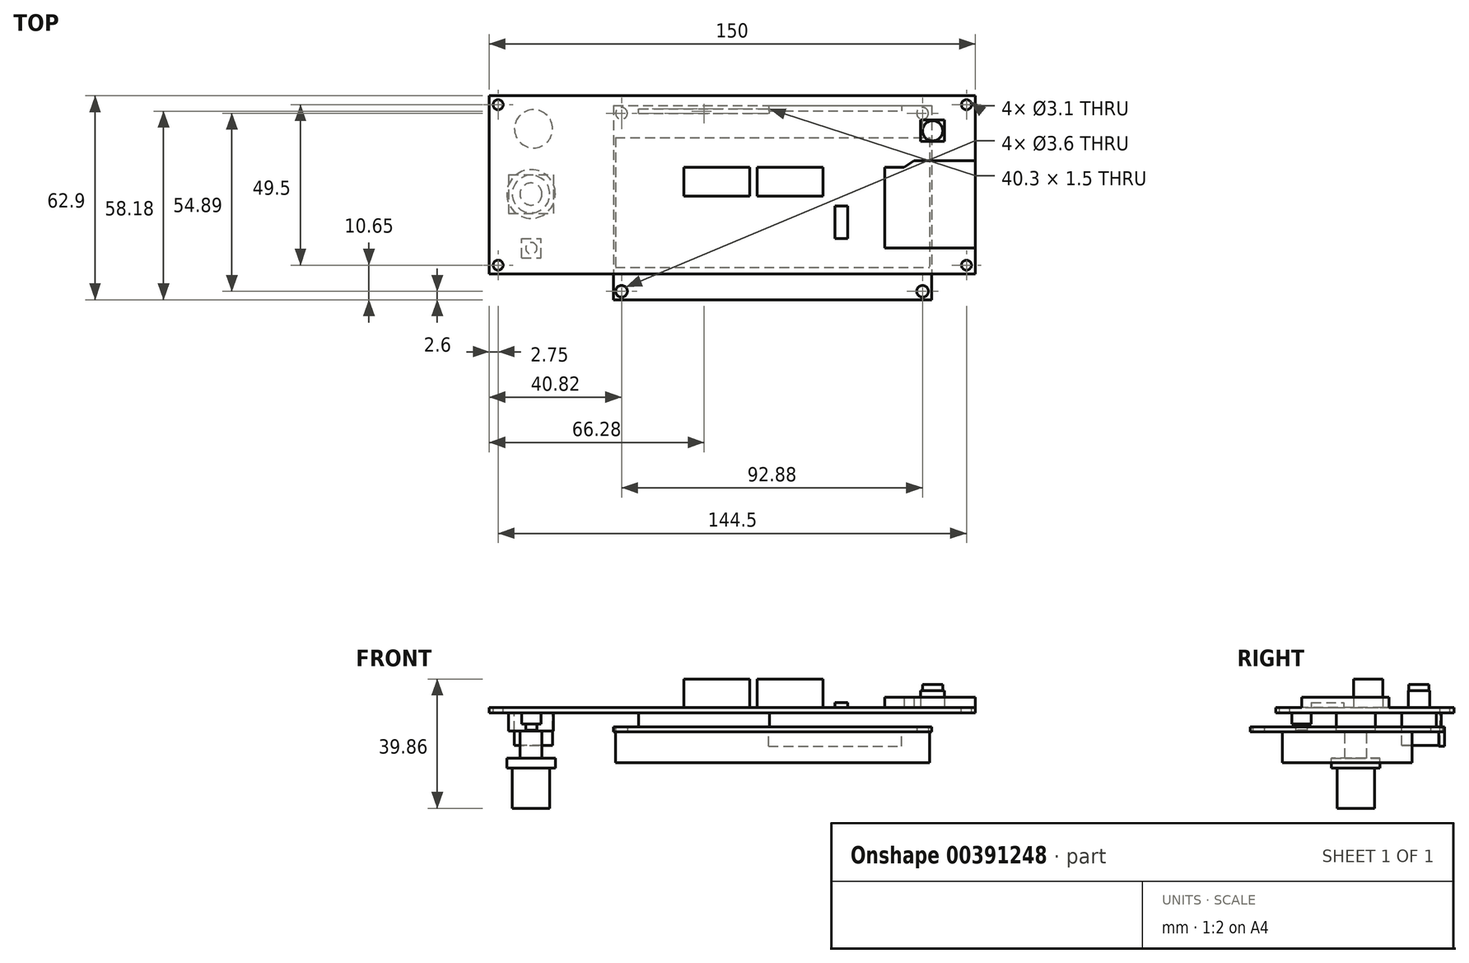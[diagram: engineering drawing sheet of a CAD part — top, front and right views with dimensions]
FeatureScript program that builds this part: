
annotation { "Feature Type Name" : "Feature", "Feature Type Description" : "" }
export const myFeature = defineFeature(function(context is Context, id is Id, definition is map)
    precondition{}
    {
        {
            var Q0;
            Q0=qCreatedBy(makeId("Top.planeOp"),FACE);
            var sketch = newSketch(context, id + "F0", { "sketchPlane" : qUnion([Q0])});
            skLineSegment(sketch, "E0.bottom", {"start": v(0, 0) * mm, "end": v(150, 0) * mm});
            skLineSegment(sketch, "E0.top", {"start": v(0, 55) * mm, "end": v(150, 55) * mm});
            skLineSegment(sketch, "E0.left", {"start": v(0, 0) * mm, "end": v(0, 55) * mm});
            skLineSegment(sketch, "E0.right", {"start": v(150, 0) * mm, "end": v(150, 55) * mm});
            skCircle(sketch, "E1", {"center": v(2.75, 52.25) * mm, "radius": 1.55 * mm});
            skCircle(sketch, "E2", {"center": v(2.75, 2.75) * mm, "radius": 1.55 * mm});
            skCircle(sketch, "E3", {"center": v(147.25, 52.25) * mm, "radius": 1.55 * mm});
            skCircle(sketch, "E4", {"center": v(147.25, 2.75) * mm, "radius": 1.55 * mm});
            skLineSegment(sketch, "E5.bottom", {"start": v(60, 24) * mm, "end": v(80.36, 24) * mm});
            skLineSegment(sketch, "E5.top", {"start": v(60, 33) * mm, "end": v(80.36, 33) * mm});
            skLineSegment(sketch, "E5.left", {"start": v(60, 24) * mm, "end": v(60, 33) * mm});
            skLineSegment(sketch, "E5.right", {"start": v(103, 24) * mm, "end": v(103, 33) * mm});
            skPoint(sketch, "E6", {"position": v(150, 8) * mm});
            skPoint(sketch, "E7", {"position": v(150, 35) * mm});
            skPoint(sketch, "E8", {"position": v(131, 35) * mm});
            skPoint(sketch, "E9", {"position": v(122, 8) * mm});
            skPoint(sketch, "E10", {"position": v(122, 33) * mm});
            skPoint(sketch, "E11", {"position": v(128, 33) * mm});
            skLineSegment(sketch, "E12", {"start": v(122, 33) * mm, "end": v(128, 33) * mm});
            skLineSegment(sketch, "E13", {"start": v(131, 35) * mm, "end": v(128, 33) * mm});
            skLineSegment(sketch, "E14", {"start": v(150, 35) * mm, "end": v(131, 35) * mm});
            skLineSegment(sketch, "E15", {"start": v(122, 33) * mm, "end": v(122, 8) * mm});
            skLineSegment(sketch, "E16", {"start": v(122, 8) * mm, "end": v(150, 8) * mm});
            skLineSegment(sketch, "E17", {"start": v(2.75, 52.25) * mm, "end": v(2.75, 2.75) * mm, "construction": true});
            skLineSegment(sketch, "E18", {"start": v(2.75, 2.75) * mm, "end": v(147.25, 2.75) * mm, "construction": true});
            skLineSegment(sketch, "E19", {"start": v(147.25, 2.75) * mm, "end": v(147.25, 52.25) * mm, "construction": true});
            skLineSegment(sketch, "E20", {"start": v(147.25, 52.25) * mm, "end": v(2.75, 52.25) * mm, "construction": true});
            skCircle(sketch, "E21", {"center": v(136.8, 44.2) * mm, "radius": 3.12 * mm});
            skLineSegment(sketch, "E22.bottom", {"start": v(140.5, 40.9) * mm, "end": v(133.1, 40.9) * mm});
            skLineSegment(sketch, "E22.top", {"start": v(140.5, 47.5) * mm, "end": v(133.1, 47.5) * mm});
            skLineSegment(sketch, "E22.left", {"start": v(140.5, 40.9) * mm, "end": v(140.5, 47.5) * mm});
            skLineSegment(sketch, "E22.right", {"start": v(133.1, 40.9) * mm, "end": v(133.1, 47.5) * mm});
            skLineSegment(sketch, "E23.bottom", {"start": v(106.7, 11) * mm, "end": v(110.6, 11) * mm});
            skLineSegment(sketch, "E23.top", {"start": v(106.7, 21) * mm, "end": v(110.6, 21) * mm});
            skLineSegment(sketch, "E23.left", {"start": v(106.7, 11) * mm, "end": v(106.7, 21) * mm});
            skLineSegment(sketch, "E23.right", {"start": v(110.6, 11) * mm, "end": v(110.6, 21) * mm});
            skLineSegment(sketch, "E24", {"start": v(80.36, 33) * mm, "end": v(80.36, 24) * mm});
            skLineSegment(sketch, "E25", {"start": v(82.64, 33) * mm, "end": v(82.64, 24) * mm});
            skLineSegment(sketch, "E26.trimOffspring", {"start": v(82.64, 33) * mm, "end": v(103, 33) * mm});
            skLineSegment(sketch, "E27.trimOffspring", {"start": v(82.64, 24) * mm, "end": v(103, 24) * mm});
            skSolve(sketch);
        }
        {
            var Q0;
            Q0 = qSketchRegion(id + "F0", true);
            var Q1;
            Q1=makeQuery(id+"F0.imprint","IMPRINT",FACE,{"disambiguationData":[TD([[makeQuery(id+"F0.imprint","IMPRINT",EDGE,{"derivedFrom":sQuery(id+"F0.wireOp",EDGE,"E5.bottom")}),1.0]])]});
            var Q2;
            Q2=makeQuery(id+"F0.imprint","IMPRINT",FACE,{"disambiguationData":[TD([[makeQuery(id+"F0.imprint","IMPRINT",EDGE,{"derivedFrom":sQuery(id+"F0.wireOp",EDGE,"E23.bottom")}),1.0]])]});
            var Q3;
            Q3=makeQuery(id+"F0.imprint","IMPRINT",FACE,{"disambiguationData":[TD([[makeQuery(id+"F0.imprint","IMPRINT",EDGE,{"derivedFrom":sQuery(id+"F0.wireOp",EDGE,"E21")}),-1.0]])]});
            var Q4;
            Q4=makeQuery(id+"F0.imprint","IMPRINT",FACE,{"disambiguationData":[TD([[makeQuery(id+"F0.imprint","IMPRINT",EDGE,{"derivedFrom":sQuery(id+"F0.wireOp",EDGE,"E21")}),1.0]])]});
            var Q5;
            Q5=makeQuery(id+"F0.imprint","IMPRINT",FACE,{"disambiguationData":[TD([[makeQuery(id+"F0.imprint","IMPRINT",EDGE,{"derivedFrom":sQuery(id+"F0.wireOp",EDGE,"E5.right")}),1.0]])]});
            extrude(context, id + "F1", {"entities" : qUnion([Q0, Q1, Q2, Q3, Q4, Q5]), "oppositeDirection" : true, "depth" : 1.6 * mm});
        }
        {
            var Q0;
            Q0=makeQuery(id+"F0.imprint","IMPRINT",FACE,{"disambiguationData":[TD([[makeQuery(id+"F0.imprint","IMPRINT",EDGE,{"derivedFrom":sQuery(id+"F0.wireOp",EDGE,"E5.bottom")}),1.0]])]});
            var Q1;
            Q1=makeQuery(id+"F0.imprint","IMPRINT",FACE,{"disambiguationData":[TD([[makeQuery(id+"F0.imprint","IMPRINT",EDGE,{"derivedFrom":sQuery(id+"F0.wireOp",EDGE,"E5.right")}),1.0]])]});
            extrude(context, id + "F2", {"entities" : qUnion([Q0, Q1]), "operationType" : NewBodyOperationType.ADD, "depth" : 8.8 * mm});
        }
        {
            var Q0;
            Q0=makeQuery(id+"F0.imprint","IMPRINT",FACE,{"disambiguationData":[TD([[makeQuery(id+"F0.imprint","IMPRINT",EDGE,{"derivedFrom":sQuery(id+"F0.wireOp",EDGE,"E12")}),-1.0]])]});
            extrude(context, id + "F3", {"entities" : qUnion([Q0]), "operationType" : NewBodyOperationType.ADD, "depth" : 3.2 * mm});
        }
        {
            var Q0;
            Q0=makeQuery(id+"F0.imprint","IMPRINT",FACE,{"disambiguationData":[TD([[makeQuery(id+"F0.imprint","IMPRINT",EDGE,{"derivedFrom":sQuery(id+"F0.wireOp",EDGE,"E23.bottom")}),1.0]])]});
            extrude(context, id + "F4", {"entities" : qUnion([Q0]), "operationType" : NewBodyOperationType.ADD, "depth" : 1.5 * mm});
        }
        {
            var Q0;
            Q0=makeQuery(id+"F0.imprint","IMPRINT",FACE,{"disambiguationData":[TD([[makeQuery(id+"F0.imprint","IMPRINT",EDGE,{"derivedFrom":sQuery(id+"F0.wireOp",EDGE,"E21")}),-1.0]])]});
            var Q1;
            Q1=makeQuery(id+"F0.imprint","IMPRINT",FACE,{"disambiguationData":[TD([[makeQuery(id+"F0.imprint","IMPRINT",EDGE,{"derivedFrom":sQuery(id+"F0.wireOp",EDGE,"E21")}),1.0]])]});
            extrude(context, id + "F5", {"entities" : qUnion([Q0, Q1]), "operationType" : NewBodyOperationType.ADD, "depth" : 5.3 * mm});
        }
        {
            var Q0;
            Q0=makeQuery(id+"F5.opExtrude","CAP_FACE",FACE,{"disambiguationData":[OSD([sQuery(id+"F0.wireOp",EDGE,"E22.bottom"),sQuery(id+"F0.wireOp",EDGE,"E22.top"),sQuery(id+"F0.wireOp",EDGE,"E22.left"),sQuery(id+"F0.wireOp",EDGE,"E22.right")])],"isStart":false});
            var sketch = newSketch(context, id + "F6", { "sketchPlane" : qUnion([Q0])});
            skCircle(sketch, "E28.1", {"center": v(136.8, 44.2) * mm, "radius": 3.12 * mm});
            skSolve(sketch);
        }
        {
            var Q0;
            Q0=makeQuery(id+"F6.imprint","IMPRINT",FACE,{"disambiguationData":[TD([[makeQuery(id+"F6.imprint","IMPRINT",EDGE,{"derivedFrom":sQuery(id+"F6.wireOp",EDGE,"E28.1")}),1.0]])]});
            extrude(context, id + "F7", {"entities" : qUnion([Q0]), "operationType" : NewBodyOperationType.ADD, "depth" : 1.87 * mm});
        }
        {
            var Q0;
            Q0=makeQuery(id+"F1.opExtrude","CAP_FACE",FACE,{"disambiguationData":[OSD([sQuery(id+"F0.wireOp",EDGE,"E0.bottom"),sQuery(id+"F0.wireOp",EDGE,"E0.top"),sQuery(id+"F0.wireOp",EDGE,"E0.left"),sQuery(id+"F0.wireOp",EDGE,"E0.right"),sQuery(id+"F0.wireOp",EDGE,"E1"),sQuery(id+"F0.wireOp",EDGE,"E2"),sQuery(id+"F0.wireOp",EDGE,"E3"),sQuery(id+"F0.wireOp",EDGE,"E4")])],"isStart":false});
            var sketch = newSketch(context, id + "F8", { "sketchPlane" : qUnion([Q0])});
            skCircle(sketch, "E29", {"center": v(13.68, -44.82) * mm, "radius": 5.88 * mm});
            skSolve(sketch);
        }
        {
            var Q0;
            Q0=makeQuery(id+"F8.imprint","IMPRINT",FACE,{"disambiguationData":[TD([[makeQuery(id+"F8.imprint","IMPRINT",EDGE,{"derivedFrom":sQuery(id+"F8.wireOp",EDGE,"E29")}),1.0]])]});
            extrude(context, id + "F9", {"entities" : qUnion([Q0]), "operationType" : NewBodyOperationType.ADD, "depth" : 10 * mm});
        }
        {
            var Q0;
            Q0=makeQuery(id+"F1.opExtrude","CAP_FACE",FACE,{"disambiguationData":[OSD([sQuery(id+"F0.wireOp",EDGE,"E0.bottom"),sQuery(id+"F0.wireOp",EDGE,"E0.top"),sQuery(id+"F0.wireOp",EDGE,"E0.left"),sQuery(id+"F0.wireOp",EDGE,"E0.right"),sQuery(id+"F0.wireOp",EDGE,"E1"),sQuery(id+"F0.wireOp",EDGE,"E2"),sQuery(id+"F0.wireOp",EDGE,"E3"),sQuery(id+"F0.wireOp",EDGE,"E4")])],"isStart":false});
            var sketch = newSketch(context, id + "F10", { "sketchPlane" : qUnion([Q0])});
            skLineSegment(sketch, "E30.bottom", {"start": v(6, -30.7) * mm, "end": v(19.8, -30.7) * mm});
            skLineSegment(sketch, "E30.top", {"start": v(6, -18.7) * mm, "end": v(19.8, -18.7) * mm});
            skLineSegment(sketch, "E30.left", {"start": v(6, -30.7) * mm, "end": v(6, -18.7) * mm});
            skLineSegment(sketch, "E30.right", {"start": v(19.8, -30.7) * mm, "end": v(19.8, -18.7) * mm});
            skLineSegment(sketch, "E31.bottom", {"start": v(10, -5) * mm, "end": v(16, -5) * mm});
            skLineSegment(sketch, "E31.top", {"start": v(10, -11) * mm, "end": v(16, -11) * mm});
            skLineSegment(sketch, "E31.left", {"start": v(10, -5) * mm, "end": v(10, -11) * mm});
            skLineSegment(sketch, "E31.right", {"start": v(16, -5) * mm, "end": v(16, -11) * mm});
            skCircle(sketch, "E32", {"center": v(13, -8) * mm, "radius": 1.75 * mm});
            skPoint(sketch, "E32.centerSnap0", {"position": v(13, -5) * mm});
            skPoint(sketch, "E32.centerSnap1", {"position": v(10, -8) * mm});
            skCircle(sketch, "E33", {"center": v(12.9, -24.7) * mm, "radius": 7.5 * mm, "construction": true});
            skPoint(sketch, "E33.centerSnap0", {"position": v(6, -24.7) * mm});
            skPoint(sketch, "E33.centerSnap1", {"position": v(12.9, -18.7) * mm});
            skCircle(sketch, "E34", {"center": v(12.9, -24.7) * mm, "radius": 5.8 * mm, "construction": true});
            skSolve(sketch);
        }
        {
            var Q0;
            Q0=makeQuery(id+"F10.imprint","IMPRINT",FACE,{"disambiguationData":[TD([[makeQuery(id+"F10.imprint","IMPRINT",EDGE,{"derivedFrom":sQuery(id+"F10.wireOp",EDGE,"E30.bottom")}),1.0]])]});
            extrude(context, id + "F11", {"entities" : qUnion([Q0]), "operationType" : NewBodyOperationType.ADD, "depth" : 5.6 * mm});
        }
        {
            var Q0;
            Q0=makeQuery(id+"F11.opExtrude","CAP_FACE",FACE,{"disambiguationData":[OSD([sQuery(id+"F10.wireOp",EDGE,"E30.bottom"),sQuery(id+"F10.wireOp",EDGE,"E30.top"),sQuery(id+"F10.wireOp",EDGE,"E30.left"),sQuery(id+"F10.wireOp",EDGE,"E30.right")])],"isStart":false});
            var sketch = newSketch(context, id + "F12", { "sketchPlane" : qUnion([Q0])});
            skCircle(sketch, "E35", {"center": v(12.9, -24.7) * mm, "radius": 3.4 * mm});
            skPoint(sketch, "E35.centerSnap0", {"position": v(6, -24.7) * mm});
            skPoint(sketch, "E35.centerSnap1", {"position": v(12.9, -18.7) * mm});
            skSolve(sketch);
        }
        {
            var Q0;
            Q0 = qSketchRegion(id + "F12", true);
            extrude(context, id + "F13", {"entities" : qUnion([Q0]), "operationType" : NewBodyOperationType.ADD, "depth" : 8.4 * mm});
        }
        {
            var Q0;
            Q0=makeQuery(id+"F13.opExtrude","CAP_FACE",FACE,{"disambiguationData":[OSD([sQuery(id+"F12.wireOp",EDGE,"E35")])],"isStart":false});
            var sketch = newSketch(context, id + "F14", { "sketchPlane" : qUnion([Q0])});
            skCircle(sketch, "E36.0", {"center": v(12.9, -24.7) * mm, "radius": 7.5 * mm});
            skSolve(sketch);
        }
        {
            var Q0;
            Q0=makeQuery(id+"F14.imprint","IMPRINT",FACE,{"disambiguationData":[TD([[makeQuery(id+"F14.imprint","IMPRINT",EDGE,{"derivedFrom":sQuery(id+"F14.wireOp",EDGE,"E36.0")}),1.0]])]});
            var Q1;
            Q1=makeQuery(id+"F14.imprint","IMPRINT",FACE,{"disambiguationData":[TD([[makeQuery(id+"F14.imprint","IMPRINT",EDGE,{"derivedFrom":makeQuery(id+"F13.opExtrude","CAP_EDGE",EDGE,{"disambiguationData":[OSD([sQuery(id+"F12.wireOp",EDGE,"E35")])],"isStart":false})}),1.0]])]});
            extrude(context, id + "F15", {"entities" : qUnion([Q0, Q1]), "operationType" : NewBodyOperationType.ADD, "depth" : 3 * mm});
        }
        {
            var Q0;
            Q0=makeQuery(id+"F15.opExtrude","CAP_FACE",FACE,{"disambiguationData":[OSD([sQuery(id+"F14.wireOp",EDGE,"E36.0")])],"isStart":false});
            var sketch = newSketch(context, id + "F16", { "sketchPlane" : qUnion([Q0])});
            skCircle(sketch, "E37.0", {"center": v(12.9, -24.7) * mm, "radius": 5.8 * mm});
            skLineSegment(sketch, "E38.0", {"start": v(0, 0) * mm, "end": v(0, -55) * mm});
            skSolve(sketch);
        }
        {
            var Q0;
            Q0 = qSketchRegion(id + "F16", true);
            extrude(context, id + "F17", {"entities" : qUnion([Q0]), "operationType" : NewBodyOperationType.ADD, "depth" : 12.45 * mm});
        }
        {
            var Q0;
            Q0=makeQuery(id+"F10.imprint","IMPRINT",FACE,{"disambiguationData":[TD([[makeQuery(id+"F10.imprint","IMPRINT",EDGE,{"derivedFrom":sQuery(id+"F10.wireOp",EDGE,"E31.bottom")}),-1.0]])]});
            var Q1;
            Q1=makeQuery(id+"F10.imprint","IMPRINT",FACE,{"disambiguationData":[TD([[makeQuery(id+"F10.imprint","IMPRINT",EDGE,{"derivedFrom":sQuery(id+"F10.wireOp",EDGE,"E32")}),1.0]])]});
            extrude(context, id + "F18", {"entities" : qUnion([Q0, Q1]), "operationType" : NewBodyOperationType.ADD, "depth" : (5.1 - 1.6) * mm});
        }
        {
            var Q0;
            Q0=makeQuery(id+"F18.opExtrude","CAP_FACE",FACE,{"disambiguationData":[OSD([sQuery(id+"F10.wireOp",EDGE,"E31.bottom"),sQuery(id+"F10.wireOp",EDGE,"E31.top"),sQuery(id+"F10.wireOp",EDGE,"E31.left"),sQuery(id+"F10.wireOp",EDGE,"E31.right")])],"isStart":false});
            var sketch = newSketch(context, id + "F19", { "sketchPlane" : qUnion([Q0])});
            skCircle(sketch, "E39.0", {"center": v(13, -8) * mm, "radius": 1.75 * mm});
            skSolve(sketch);
        }
        {
            var Q0;
            Q0 = qSketchRegion(id + "F19", true);
            extrude(context, id + "F20", {"entities" : qUnion([Q0]), "operationType" : NewBodyOperationType.ADD, "depth" : 1.85 * mm});
        }
        {
            var Q0;
            Q0=makeQuery(id+"F10.imprint","IMPRINT",FACE,{"disambiguationData":[TD([[makeQuery(id+"F10.imprint","IMPRINT",EDGE,{"derivedFrom":sQuery(id+"F10.wireOp",EDGE,"E30.bottom")}),-1.0]])]});
            cPlane(context, id + "F21", {"entities" : qUnion([Q0]), "cplaneType" : CPlaneType.OFFSET, "offset" : 5.9 * mm, "width" : 150 * mm, "height" : 150 * mm});
        }
        {
            var Q0;
            Q0=qCreatedBy(id+"F21.planeOp",FACE);
            var sketch = newSketch(context, id + "F22", { "sketchPlane" : qUnion([Q0])});
            skLineSegment(sketch, "E40.bottom", {"start": v(38.33, -52.03) * mm, "end": v(136.5, -52.03) * mm});
            skLineSegment(sketch, "E40.top", {"start": v(38.33, 7.9) * mm, "end": v(136.5, 7.9) * mm});
            skLineSegment(sketch, "E40.left", {"start": v(38.33, -52.03) * mm, "end": v(38.33, 7.9) * mm});
            skLineSegment(sketch, "E40.right", {"start": v(136.5, -52.03) * mm, "end": v(136.5, 7.9) * mm});
            skCircle(sketch, "E41", {"center": v(40.82, -49.6) * mm, "radius": 1.8 * mm});
            skCircle(sketch, "E42", {"center": v(40.82, 5.3) * mm, "radius": 1.8 * mm});
            skCircle(sketch, "E43", {"center": v(133.7, 5.3) * mm, "radius": 1.8 * mm});
            skCircle(sketch, "E44", {"center": v(133.7, -49.59) * mm, "radius": 1.8 * mm});
            skLineSegment(sketch, "E45.bottom", {"start": v(46.13, -49.53) * mm, "end": v(86.43, -49.53) * mm});
            skLineSegment(sketch, "E45.top", {"start": v(46.13, -51.03) * mm, "end": v(86.43, -51.03) * mm});
            skLineSegment(sketch, "E45.left", {"start": v(46.13, -49.53) * mm, "end": v(46.13, -51.03) * mm});
            skLineSegment(sketch, "E45.right", {"start": v(86.43, -49.53) * mm, "end": v(86.43, -51.03) * mm});
            skSolve(sketch);
        }
        {
            var Q0;
            Q0=makeQuery(id+"F22.imprint","IMPRINT",FACE,{"disambiguationData":[TD([[makeQuery(id+"F22.imprint","IMPRINT",EDGE,{"derivedFrom":sQuery(id+"F22.wireOp",EDGE,"E45.bottom")}),-1.0]])]});
            var Q1;
            Q1=makeQuery(id+"F1.opExtrude","CAP_FACE",FACE,{"disambiguationData":[OSD([sQuery(id+"F0.wireOp",EDGE,"E0.bottom"),sQuery(id+"F0.wireOp",EDGE,"E0.top"),sQuery(id+"F0.wireOp",EDGE,"E0.left"),sQuery(id+"F0.wireOp",EDGE,"E0.right"),sQuery(id+"F0.wireOp",EDGE,"E1"),sQuery(id+"F0.wireOp",EDGE,"E2"),sQuery(id+"F0.wireOp",EDGE,"E3"),sQuery(id+"F0.wireOp",EDGE,"E4")])],"isStart":false});
            extrude(context, id + "F23", {"entities" : qUnion([Q0]), "operationType" : NewBodyOperationType.ADD, "endBound" : BoundingType.UP_TO_SURFACE, "oppositeDirection" : true, "endBoundEntityFace" : qUnion([Q1]), "depth" : 1.6 * mm});
        }
        {
            var Q0;
            Q0 = qSketchRegion(id + "F22", true);
            extrude(context, id + "F24", {"entities" : qUnion([Q0]), "operationType" : NewBodyOperationType.ADD, "oppositeDirection" : true, "depth" : 1.6 * mm});
        }
        {
            var Q0;
            {var subQ0=sQuery(id+"F22.wireOp",EDGE,"E45.right");var subQ1=sQuery(id+"F22.wireOp",EDGE,"E45.left");var subQ2=sQuery(id+"F22.wireOp",EDGE,"E45.top");var subQ3=sQuery(id+"F22.wireOp",EDGE,"E45.bottom");Q0=makeQuery(id+"F24.boolean.opBoolean","MERGE",FACE,{"derivedFrom":[makeQuery(id+"F23.opExtrude","CAP_FACE",FACE,{"disambiguationData":[OSD([subQ3,subQ2,subQ1,subQ0])],"isStart":true}),makeQuery(id+"F24.opExtrude","CAP_FACE",FACE,{"disambiguationData":[OSD([sQuery(id+"F22.wireOp",EDGE,"E40.bottom"),sQuery(id+"F22.wireOp",EDGE,"E40.top"),sQuery(id+"F22.wireOp",EDGE,"E40.left"),sQuery(id+"F22.wireOp",EDGE,"E40.right"),sQuery(id+"F22.wireOp",EDGE,"E41"),sQuery(id+"F22.wireOp",EDGE,"E42"),sQuery(id+"F22.wireOp",EDGE,"E43"),sQuery(id+"F22.wireOp",EDGE,"E44"),subQ3,subQ2,subQ1,subQ0])],"isStart":true})]});}
            var sketch = newSketch(context, id + "F25", { "sketchPlane" : qUnion([Q0])});
            skLineSegment(sketch, "E46.bottom", {"start": v(38.91, -42.1) * mm, "end": v(135.91, -42.1) * mm});
            skLineSegment(sketch, "E46.top", {"start": v(38.91, -2.1) * mm, "end": v(135.91, -2.1) * mm});
            skLineSegment(sketch, "E46.left", {"start": v(38.91, -42.1) * mm, "end": v(38.91, -2.1) * mm});
            skLineSegment(sketch, "E46.right", {"start": v(135.91, -42.1) * mm, "end": v(135.91, -2.1) * mm});
            skPoint(sketch, "E47", {"position": v(87.41, -2.1) * mm});
            skPoint(sketch, "E48", {"position": v(87.41, -42.1) * mm});
            skPoint(sketch, "E49", {"position": v(87.41, 7.9) * mm});
            skPoint(sketch, "E50", {"position": v(87.41, -52.03) * mm});
            skLineSegment(sketch, "E51.bottom", {"start": v(86.2, -52.03) * mm, "end": v(127.2, -52.03) * mm});
            skLineSegment(sketch, "E51.top", {"start": v(86.2, -50.33) * mm, "end": v(127.2, -50.33) * mm});
            skLineSegment(sketch, "E51.left", {"start": v(86.2, -52.03) * mm, "end": v(86.2, -50.33) * mm});
            skLineSegment(sketch, "E51.right", {"start": v(127.2, -52.03) * mm, "end": v(127.2, -50.33) * mm});
            skSolve(sketch);
        }
        {
            var Q0;
            Q0=makeQuery(id+"F25.imprint","IMPRINT",FACE,{"disambiguationData":[TD([[makeQuery(id+"F25.imprint","IMPRINT",EDGE,{"derivedFrom":sQuery(id+"F25.wireOp",EDGE,"E51.bottom")}),1.0]])]});
            extrude(context, id + "F26", {"entities" : qUnion([Q0]), "operationType" : NewBodyOperationType.ADD, "depth" : 4.4 * mm});
        }
        {
            var Q0;
            Q0=makeQuery(id+"F25.imprint","IMPRINT",FACE,{"disambiguationData":[TD([[makeQuery(id+"F25.imprint","IMPRINT",EDGE,{"derivedFrom":sQuery(id+"F25.wireOp",EDGE,"E46.bottom")}),1.0]])]});
            extrude(context, id + "F27", {"entities" : qUnion([Q0]), "operationType" : NewBodyOperationType.ADD, "depth" : 9.5 * mm});
        }
    });
